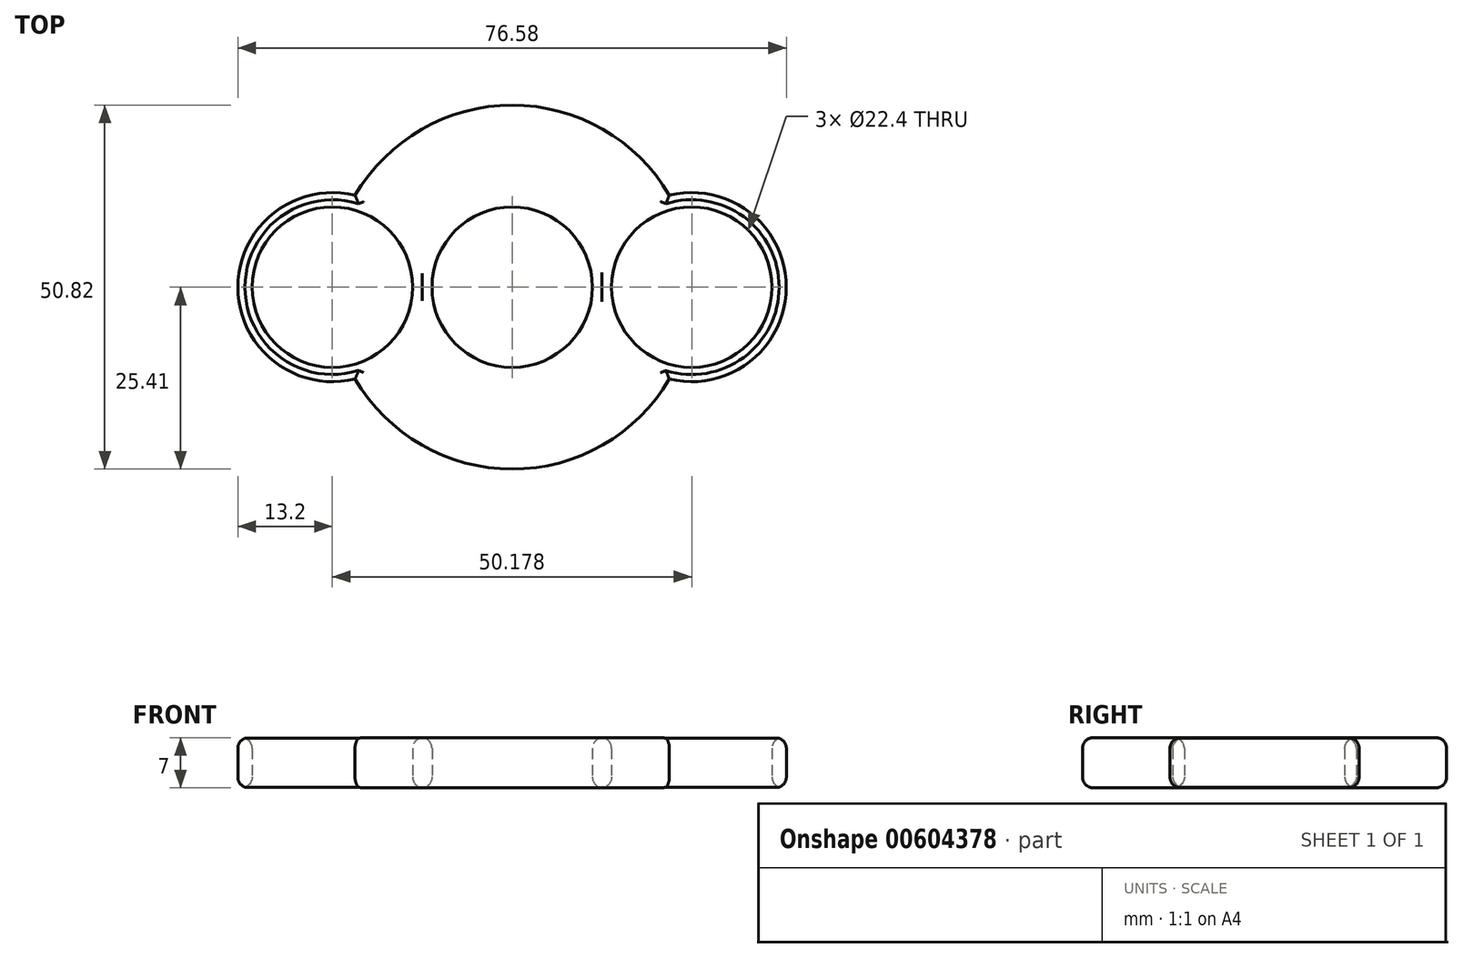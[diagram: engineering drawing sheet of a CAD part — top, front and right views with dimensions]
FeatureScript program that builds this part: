
annotation { "Feature Type Name" : "Feature", "Feature Type Description" : "" }
export const myFeature = defineFeature(function(context is Context, id is Id, definition is map)
    precondition{}
    {
        {
            var Q0;
            Q0=qCreatedBy(makeId("Top.planeOp"),FACE);
            var sketch = newSketch(context, id + "F0", { "sketchPlane" : qUnion([Q0])});
            skCircle(sketch, "E0", {"center": v(0, 0) * mm, "radius": 11.2 * mm});
            skCircle(sketch, "E1", {"center": v(25.07, 0) * mm, "radius": 11.2 * mm});
            skCircle(sketch, "E2", {"center": v(-25.1, 0) * mm, "radius": 11.2 * mm});
            skArc(sketch, "E3", {"start": v(-21.94, 12.81) * mm, "mid": v(-38.3, 0) * mm, "end": v(-21.94, -12.81) * mm});
            skArc(sketch, "E4", {"start": v(-22.91, -10.98) * mm, "mid": v(0, -25.41) * mm, "end": v(22.91, -11) * mm});
            skArc(sketch, "E5.trimOffspring", {"start": v(21.94, -12.82) * mm, "mid": v(38.27, 0) * mm, "end": v(21.94, 12.82) * mm});
            skArc(sketch, "E6.trimOffspring", {"start": v(22.91, 11) * mm, "mid": v(0, 25.41) * mm, "end": v(-22.91, 10.98) * mm});
            skSolve(sketch);
        }
        {
            var Q0;
            Q0=makeQuery(id+"F0.imprint","IMPRINT",FACE,{"disambiguationData":[TD([[makeQuery(id+"F0.imprint","IMPRINT",EDGE,{"derivedFrom":sQuery(id+"F0.wireOp",EDGE,"E0")}),-1.0]])]});
            var Q1;
            {var subQ5=sQuery(id+"F0.wireOp",EDGE,"E5.trimOffspring");Q1=makeQuery(id+"F0.imprint","IMPRINT",FACE,{"disambiguationData":[TD([[makeQuery(id+"F0.imprint","IMPRINT",EDGE,{"derivedFrom":subQ5}),1.0]])]});}
            var Q2;
            {var subQ5=sQuery(id+"F0.wireOp",EDGE,"E3");Q2=makeQuery(id+"F0.imprint","IMPRINT",FACE,{"disambiguationData":[TD([[makeQuery(id+"F0.imprint","IMPRINT",EDGE,{"derivedFrom":subQ5}),1.0]])]});}
            extrude(context, id + "F1", {"entities" : qUnion([Q0, Q1, Q2]), "depth" : 7 * mm, "offsetDistance" : 25 * mm});
        }
        {
            var Q0;
            Q0=makeQuery(id+"F1.opExtrude","CAP_FACE",FACE,{"disambiguationData":[OSD([sQuery(id+"F0.wireOp",EDGE,"E0"),sQuery(id+"F0.wireOp",EDGE,"E1"),sQuery(id+"F0.wireOp",EDGE,"E2"),sQuery(id+"F0.wireOp",EDGE,"E3"),sQuery(id+"F0.wireOp",EDGE,"E4"),sQuery(id+"F0.wireOp",EDGE,"E5.trimOffspring"),sQuery(id+"F0.wireOp",EDGE,"E6.trimOffspring")])],"isStart":false});
            fillet(context, id + "F2", {"entities" : qUnion([Q0]), "radius" : 1.5 * mm, "tangentPropagation" : true, "allowEdgeOverflow" : false});
        }
        {
            var Q0;
            Q0=makeQuery(id+"F1.opExtrude","CAP_FACE",FACE,{"disambiguationData":[OSD([sQuery(id+"F0.wireOp",EDGE,"E0"),sQuery(id+"F0.wireOp",EDGE,"E1"),sQuery(id+"F0.wireOp",EDGE,"E2"),sQuery(id+"F0.wireOp",EDGE,"E3"),sQuery(id+"F0.wireOp",EDGE,"E4"),sQuery(id+"F0.wireOp",EDGE,"E5.trimOffspring"),sQuery(id+"F0.wireOp",EDGE,"E6.trimOffspring")])],"isStart":true});
            fillet(context, id + "F3", {"entities" : qUnion([Q0]), "radius" : 1.5 * mm, "tangentPropagation" : true, "allowEdgeOverflow" : false});
        }
    });
